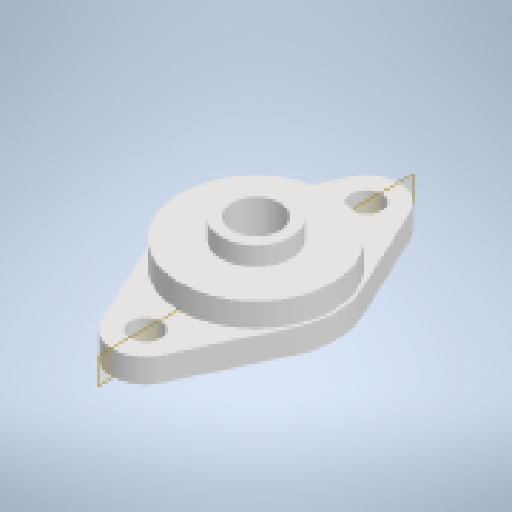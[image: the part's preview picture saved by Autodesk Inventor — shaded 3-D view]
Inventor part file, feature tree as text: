
AUTODESK INVENTOR PART (.ipt)
format: ipt  version: 2025 (Build 290162000, 162)  size: 300,544 bytes
history: native  units: in
note: dims shown in document units (in); Inventor stores cm internally (conversion verified against a paired STEP export)
features: extrude x3, sketch x3, plane x1
ambient origin geometry x8: Origin, YZ Plane, XZ Plane, XY Plane, X Axis, Y Axis, Z Axis, Center Point
bodies: Solid1 (feature_tree)
feature tree (7):
  extrude  "Extrusion1"  Depth=0.7224in
  extrude  "Extrusion2"  Depth=0.7224in
  extrude  "Extrusion3"  Depth=0.315in
  plane  "Work Plane1"
  sketch  "Sketch1"  dims[d0=1.0472in d1=0.4331in d2=0.7224in]
  sketch  "Sketch2"  dims[d3=0.4331in d4=0.7224in d5=0.1969in]
  sketch  "Sketch3"  dims[d6=0.1969in d7=0.315in d8=0.4567in d9=1.0039in d10=0.0in d12=0.0in d13=0.437in d14=0.0in d15=0.7224in d16=0.7224in d17=0.1969in d18=0.1969in d19=0.315in d20=0.4567in d21=1.0039in d22=0.0in d23=0.0in d24=0.0in d25=0.0in d26=0.315in d27=0.0in d28=0.7224in d29=0.7224in d30=0.1969in d31=0.1969in d32=0.315in d35=0.0in d36=0.0in d37=0.0in d38=0.0in d39=0.1575in d40=0.0in d41=0.0197in d42=0.0344in]
